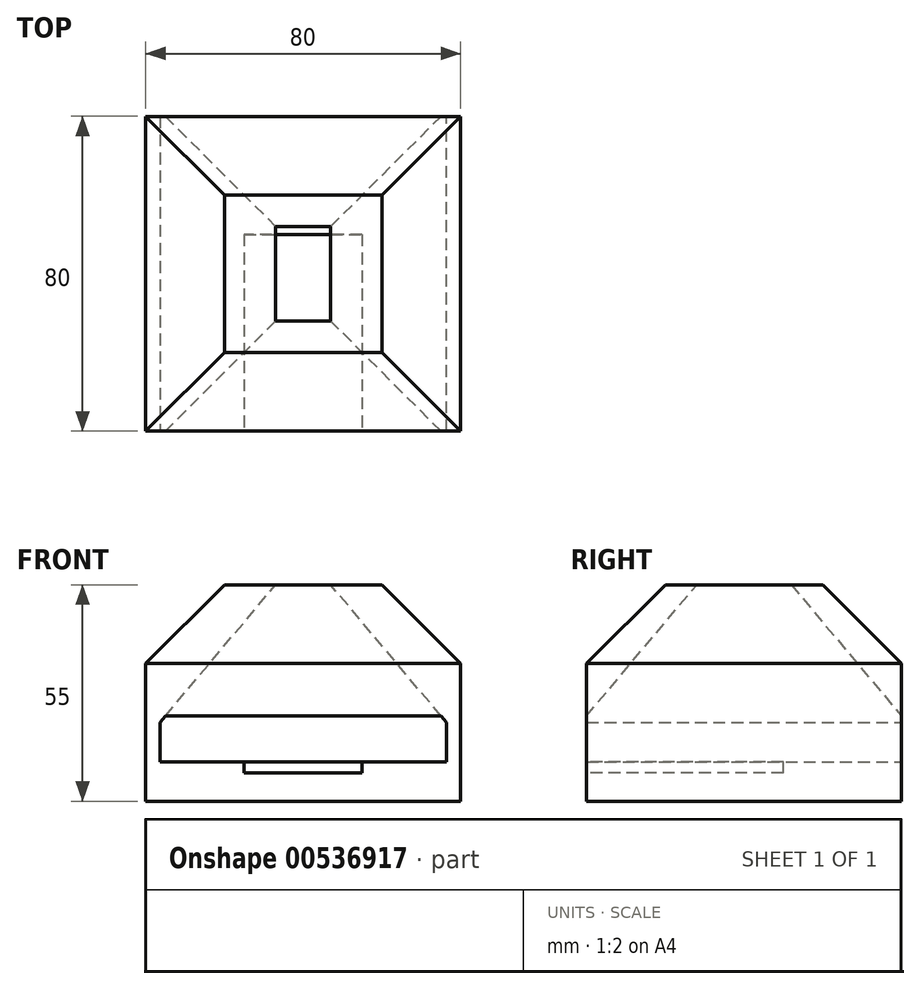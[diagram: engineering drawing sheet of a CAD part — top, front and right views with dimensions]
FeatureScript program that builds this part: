
annotation { "Feature Type Name" : "Feature", "Feature Type Description" : "" }
export const myFeature = defineFeature(function(context is Context, id is Id, definition is map)
    precondition{}
    {
        {
            var Q0;
            Q0=qCreatedBy(makeId("Top.planeOp"),FACE);
            var sketch = newSketch(context, id + "F0", { "sketchPlane" : qUnion([Q0])});
            skLineSegment(sketch, "E0.bottom", {"start": v(-36.55, 36.96) * mm, "end": v(43.45, 36.96) * mm});
            skLineSegment(sketch, "E0.top", {"start": v(-36.55, -43.04) * mm, "end": v(43.45, -43.04) * mm});
            skLineSegment(sketch, "E0.left", {"start": v(-36.55, 36.96) * mm, "end": v(-36.55, -43.04) * mm});
            skLineSegment(sketch, "E0.right", {"start": v(43.45, 36.96) * mm, "end": v(43.45, -43.04) * mm});
            skSolve(sketch);
        }
        {
            var Q0;
            Q0=makeQuery(id+"F0.imprint","IMPRINT",FACE,{"disambiguationData":[TD([[makeQuery(id+"F0.imprint","IMPRINT",EDGE,{"derivedFrom":sQuery(id+"F0.wireOp",EDGE,"E0.bottom")}),-1.0]])]});
            var Q1;
            Q1 = qSketchRegion(id + "F3", true);
            extrude(context, id + "F1", {"entities" : qUnion([Q0, Q1]), "depth" : 55 * mm, "offsetDistance" : 25 * mm});
        }
        {
            var Q0;
            Q0=makeQuery(id+"F1.opExtrude","CAP_FACE",FACE,{"disambiguationData":[OSD([sQuery(id+"F0.wireOp",EDGE,"E0.bottom"),sQuery(id+"F0.wireOp",EDGE,"E0.top"),sQuery(id+"F0.wireOp",EDGE,"E0.left"),sQuery(id+"F0.wireOp",EDGE,"E0.right")])],"isStart":false});
            chamfer(context, id + "F2", {"entities" : qUnion([Q0]), "chamferType" : ChamferType.OFFSET_ANGLE, "width" : 20 * mm, "oppositeDirection" : false, "angle" : 45 * degree, "tangentPropagation" : true});
        }
        {
            var Q0;
            Q0=makeQuery(id+"F1.opExtrude","CAP_FACE",FACE,{"disambiguationData":[OSD([sQuery(id+"F0.wireOp",EDGE,"E0.bottom"),sQuery(id+"F0.wireOp",EDGE,"E0.top"),sQuery(id+"F0.wireOp",EDGE,"E0.left"),sQuery(id+"F0.wireOp",EDGE,"E0.right")])],"isStart":false});
            var sketch = newSketch(context, id + "F3", { "sketchPlane" : qUnion([Q0])});
            skLineSegment(sketch, "E1.bottom", {"start": v(10.45, 8.96) * mm, "end": v(-3.55, 8.96) * mm});
            skLineSegment(sketch, "E1.top", {"start": v(10.45, -15.04) * mm, "end": v(-3.55, -15.04) * mm});
            skLineSegment(sketch, "E1.left", {"start": v(10.45, 8.96) * mm, "end": v(10.45, -15.04) * mm});
            skLineSegment(sketch, "E1.right", {"start": v(-3.55, 8.96) * mm, "end": v(-3.55, -15.04) * mm});
            skSolve(sketch);
        }
        {
            var Q0;
            Q0=makeQuery(id+"F3.imprint","IMPRINT",FACE,{"disambiguationData":[TD([[makeQuery(id+"F3.imprint","IMPRINT",EDGE,{"derivedFrom":sQuery(id+"F3.wireOp",EDGE,"E1.bottom")}),1.0]])]});
            extrude(context, id + "F4", {"entities" : qUnion([Q0]), "operationType" : NewBodyOperationType.REMOVE, "oppositeDirection" : true, "depth" : 35 * mm, "offsetDistance" : 25 * mm, "hasDraft" : true, "draftAngle" : 40 * degree, "hasSecondDirectionDraft" : true, "secondDirectionDraftAngle" : 0 * degree});
        }
        {
            var Q0;
            Q0=makeQuery(id+"F1.opExtrude","SWEPT_FACE",FACE,{"disambiguationData":[OSD([sQuery(id+"F0.wireOp",EDGE,"E0.top")])]});
            var sketch = newSketch(context, id + "F5", { "sketchPlane" : qUnion([Q0])});
            skLineSegment(sketch, "E2", {"start": v(-36.55, 17.5) * mm, "end": v(43.45, 17.5) * mm});
            skLineSegment(sketch, "E3", {"start": v(3.45, 35) * mm, "end": v(3.45, 0) * mm});
            skPoint(sketch, "E4", {"position": v(3.45, 17.5) * mm});
            skLineSegment(sketch, "E5.bottom", {"start": v(18.45, 22.78) * mm, "end": v(-11.55, 22.78) * mm});
            skLineSegment(sketch, "E5.top", {"start": v(18.45, 12.22) * mm, "end": v(-11.55, 12.22) * mm});
            skLineSegment(sketch, "E5.left", {"start": v(18.45, 22.78) * mm, "end": v(18.45, 12.22) * mm});
            skLineSegment(sketch, "E5.right", {"start": v(-11.55, 22.78) * mm, "end": v(-11.55, 12.22) * mm});
            skSolve(sketch);
        }
        {
            var Q0;
            {var subQ0=sQuery(id+"F5.wireOp",EDGE,"E3");var subQ1=sQuery(id+"F5.wireOp",EDGE,"E2");var subQ2=makeQuery(id+"F5.imprint","INTERSECT",VERTEX,{"derivedFrom":[subQ1,subQ0]});Q0=makeQuery(id+"F5.imprint","IMPRINT",FACE,{"disambiguationData":[TD([[makeQuery(id+"F5.imprint","IMPRINT",EDGE,{"disambiguationData":[TD([[subQ2,-1.0]])],"derivedFrom":subQ1}),1.0]])]});}
            var Q1;
            {var subQ0=sQuery(id+"F5.wireOp",EDGE,"E5.right");var subQ1=sQuery(id+"F5.wireOp",EDGE,"E2");var subQ2=makeQuery(id+"F5.imprint","INTERSECT",VERTEX,{"derivedFrom":[subQ1,subQ0]});Q1=makeQuery(id+"F5.imprint","IMPRINT",FACE,{"disambiguationData":[TD([[makeQuery(id+"F5.imprint","IMPRINT",EDGE,{"disambiguationData":[TD([[subQ2,-1.0]])],"derivedFrom":subQ1}),1.0]])]});}
            var Q2;
            {var subQ0=sQuery(id+"F5.wireOp",EDGE,"E5.right");var subQ1=sQuery(id+"F5.wireOp",EDGE,"E2");var subQ2=makeQuery(id+"F5.imprint","INTERSECT",VERTEX,{"derivedFrom":[subQ1,subQ0]});Q2=makeQuery(id+"F5.imprint","IMPRINT",FACE,{"disambiguationData":[TD([[makeQuery(id+"F5.imprint","IMPRINT",EDGE,{"disambiguationData":[TD([[subQ2,-1.0]])],"derivedFrom":subQ1}),-1.0]])]});}
            var Q3;
            {var subQ0=sQuery(id+"F5.wireOp",EDGE,"E3");var subQ1=sQuery(id+"F5.wireOp",EDGE,"E2");var subQ2=makeQuery(id+"F5.imprint","INTERSECT",VERTEX,{"derivedFrom":[subQ1,subQ0]});Q3=makeQuery(id+"F5.imprint","IMPRINT",FACE,{"disambiguationData":[TD([[makeQuery(id+"F5.imprint","IMPRINT",EDGE,{"disambiguationData":[TD([[subQ2,-1.0]])],"derivedFrom":subQ1}),-1.0]])]});}
            extrude(context, id + "F6", {"entities" : qUnion([Q0, Q1, Q2, Q3]), "operationType" : NewBodyOperationType.REMOVE, "oppositeDirection" : true, "depth" : 50 * mm, "offsetDistance" : 25 * mm});
        }
        {
            var Q0;
            Q0=makeQuery(id+"F4.boolean.opBoolean","COPY",FACE,{"derivedFrom":makeQuery(id+"F4.opExtrude","CAP_FACE",FACE,{"disambiguationData":[OSD([sQuery(id+"F3.wireOp",EDGE,"E1.bottom"),sQuery(id+"F3.wireOp",EDGE,"E1.top"),sQuery(id+"F3.wireOp",EDGE,"E1.left"),sQuery(id+"F3.wireOp",EDGE,"E1.right")])],"isStart":false})});
            extrude(context, id + "F7", {"entities" : qUnion([Q0]), "operationType" : NewBodyOperationType.REMOVE, "oppositeDirection" : true, "depth" : 10 * mm, "offsetDistance" : 25 * mm});
        }
        {
            var Q0;
            Q0=makeQuery(id+"F6.boolean.opBoolean","COPY",FACE,{"derivedFrom":makeQuery(id+"F6.opExtrude","SWEPT_FACE",FACE,{"disambiguationData":[OSD([sQuery(id+"F5.wireOp",EDGE,"E5.top")])]})});
            extrude(context, id + "F8", {"entities" : qUnion([Q0]), "operationType" : NewBodyOperationType.REMOVE, "oppositeDirection" : true, "depth" : 5 * mm, "offsetDistance" : 25 * mm});
        }
    });
